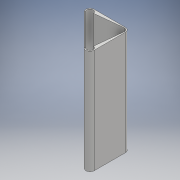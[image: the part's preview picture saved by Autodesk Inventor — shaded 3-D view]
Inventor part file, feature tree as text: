
AUTODESK INVENTOR PART (.ipt)
format: ipt  version: 2017 (Build 210142000, 142)  size: 111,616 bytes
history: native  units: mm
features: extrude x1, sketch x1
ambient origin geometry x8: Origin, YZ Plane, XZ Plane, XY Plane, X Axis, Y Axis, Z Axis, Center Point
bodies: Body1 (feature_tree)
feature tree (2):
  extrude  "Extrusion2"  Depth=100.0mm
  sketch  "Sketch2"  dims[d18=6.2mm d19=6.2mm d22=8.0mm d24=135.0deg d25=100.0mm d26=0.0mm]
